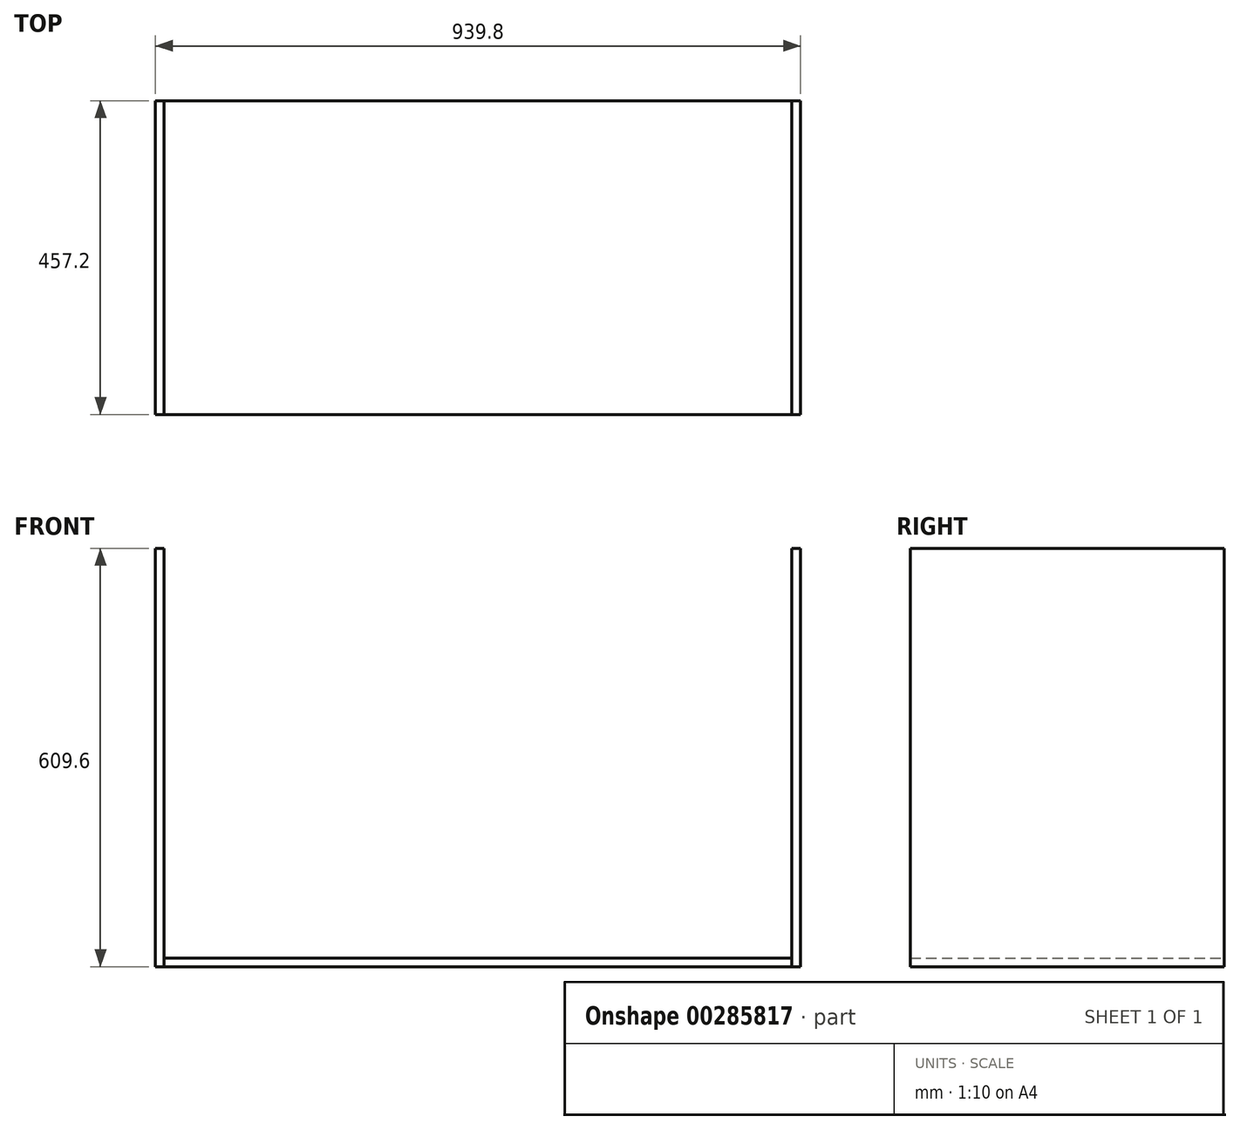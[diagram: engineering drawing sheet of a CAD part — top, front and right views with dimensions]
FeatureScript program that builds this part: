
annotation { "Feature Type Name" : "Feature", "Feature Type Description" : "" }
export const myFeature = defineFeature(function(context is Context, id is Id, definition is map)
    precondition{}
    {
        {
            var Q0;
            Q0=qCreatedBy(makeId("Front.planeOp"),FACE);
            var sketch = newSketch(context, id + "F0", { "sketchPlane" : qUnion([Q0])});
            skLineSegment(sketch, "E0.bottom", {"start": v(0, 0) * mm, "end": v(914.4, 0) * mm});
            skLineSegment(sketch, "E0.top", {"start": v(0, 12.7) * mm, "end": v(914.4, 12.7) * mm});
            skLineSegment(sketch, "E0.left", {"start": v(0, 0) * mm, "end": v(0, 12.7) * mm});
            skLineSegment(sketch, "E0.right", {"start": v(914.4, 0) * mm, "end": v(914.4, 12.7) * mm});
            skSolve(sketch);
        }
        {
            var Q0;
            Q0=makeQuery(id+"F0.imprint","IMPRINT",FACE,{"disambiguationData":[TD([[makeQuery(id+"F0.imprint","IMPRINT",EDGE,{"derivedFrom":sQuery(id+"F0.wireOp",EDGE,"E0.bottom")}),1.0]])]});
            extrude(context, id + "F1", {"entities" : qUnion([Q0]), "depth" : 457.2 * mm});
        }
        {
            var Q0;
            Q0=qCreatedBy(makeId("Front.planeOp"),FACE);
            var sketch = newSketch(context, id + "F2", { "sketchPlane" : qUnion([Q0])});
            skLineSegment(sketch, "E1.bottom", {"start": v(0, 0) * mm, "end": v(-12.7, 0) * mm});
            skLineSegment(sketch, "E1.top", {"start": v(0, 609.6) * mm, "end": v(-12.7, 609.6) * mm});
            skLineSegment(sketch, "E1.left", {"start": v(0, 0) * mm, "end": v(0, 609.6) * mm});
            skLineSegment(sketch, "E1.right", {"start": v(-12.7, 0) * mm, "end": v(-12.7, 609.6) * mm});
            skLineSegment(sketch, "E2.bottom", {"start": v(914.4, 0) * mm, "end": v(927.1, 0) * mm});
            skLineSegment(sketch, "E2.top", {"start": v(914.4, 609.6) * mm, "end": v(927.1, 609.6) * mm});
            skLineSegment(sketch, "E2.left", {"start": v(914.4, 0) * mm, "end": v(914.4, 609.6) * mm});
            skLineSegment(sketch, "E2.right", {"start": v(927.1, 0) * mm, "end": v(927.1, 609.6) * mm});
            skSolve(sketch);
        }
        {
            var Q0;
            Q0 = qSketchRegion(id + "F2", true);
            extrude(context, id + "F3", {"entities" : qUnion([Q0]), "depth" : 457.2 * mm});
        }
    });
